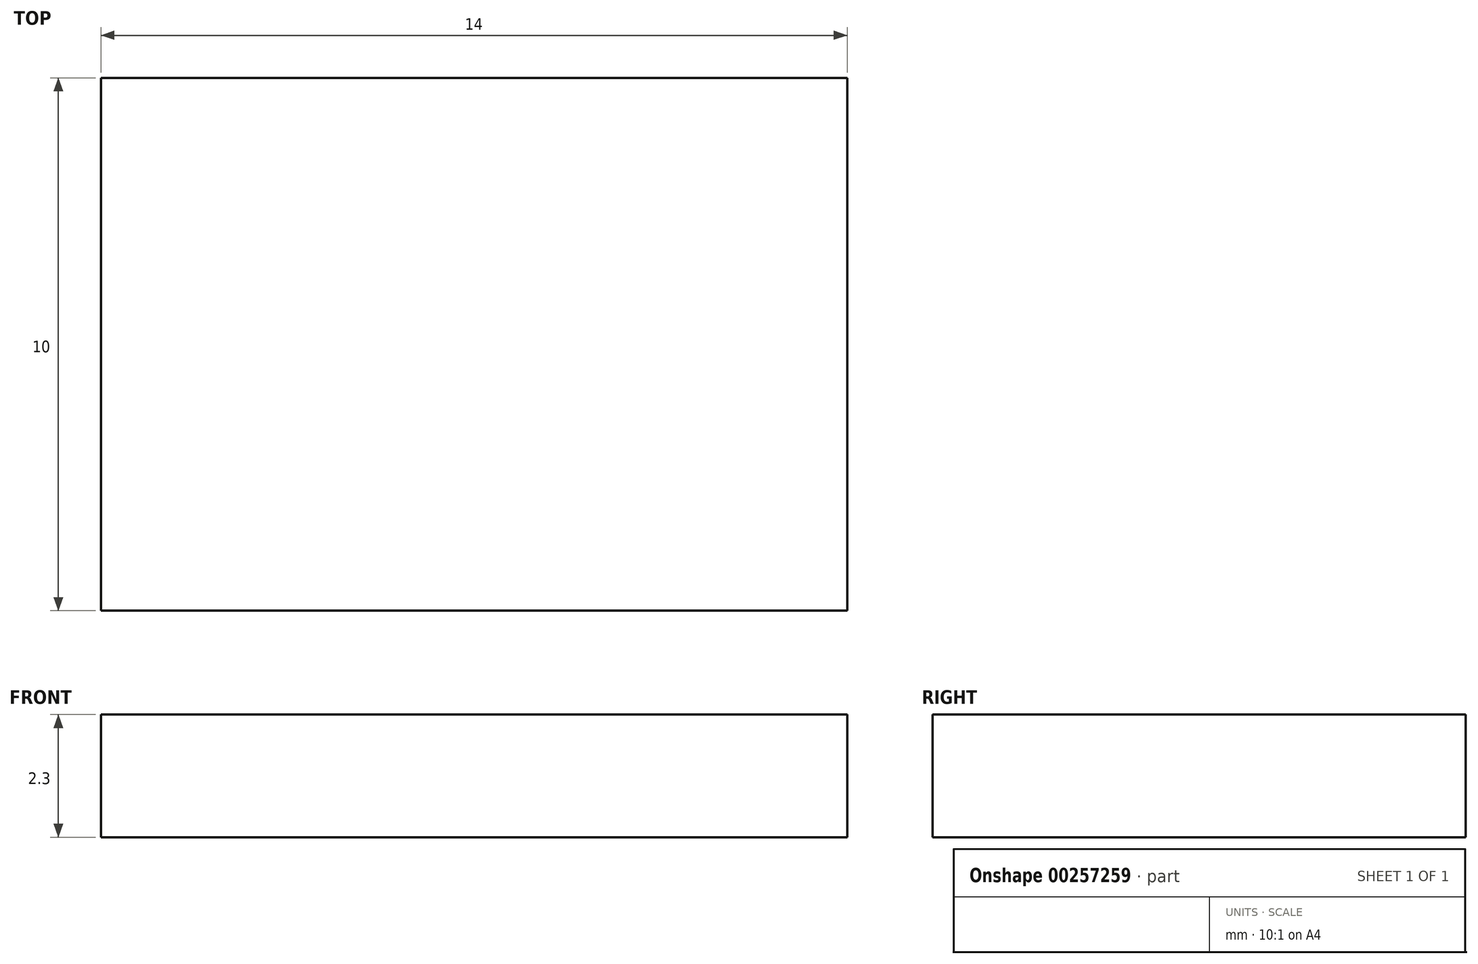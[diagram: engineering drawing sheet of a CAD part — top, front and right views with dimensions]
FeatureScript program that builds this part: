
annotation { "Feature Type Name" : "Feature", "Feature Type Description" : "" }
export const myFeature = defineFeature(function(context is Context, id is Id, definition is map)
    precondition{}
    {
        {
            var Q0;
            Q0=qCreatedBy(makeId("Top.planeOp"),FACE);
            var sketch = newSketch(context, id + "F0", { "sketchPlane" : qUnion([Q0])});
            skLineSegment(sketch, "E0.bottom", {"start": v(0, 0) * mm, "end": v(14, 0) * mm});
            skLineSegment(sketch, "E0.top", {"start": v(0, 10) * mm, "end": v(14, 10) * mm});
            skLineSegment(sketch, "E0.left", {"start": v(0, 0) * mm, "end": v(0, 10) * mm});
            skLineSegment(sketch, "E0.right", {"start": v(14, 0) * mm, "end": v(14, 10) * mm});
            skSolve(sketch);
        }
        {
            var Q0;
            Q0 = qSketchRegion(id + "F0", true);
            extrude(context, id + "F1", {"entities" : qUnion([Q0]), "depth" : 2.3 * mm});
        }
    });
